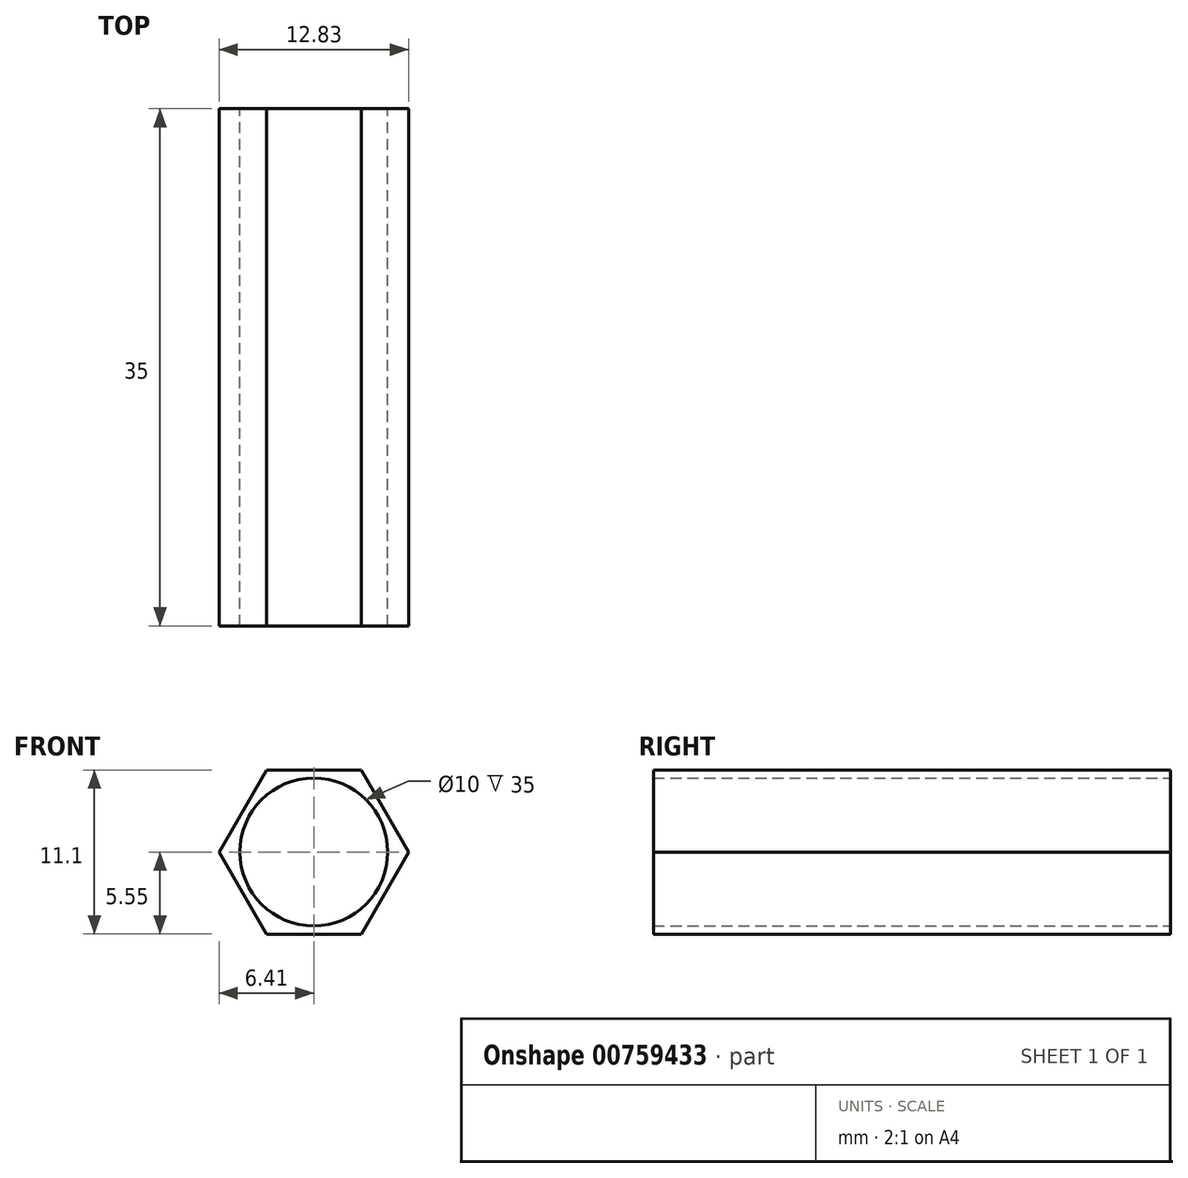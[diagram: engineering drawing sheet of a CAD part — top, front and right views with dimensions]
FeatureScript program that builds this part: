
annotation { "Feature Type Name" : "Feature", "Feature Type Description" : "" }
export const myFeature = defineFeature(function(context is Context, id is Id, definition is map)
    precondition{}
    {
        {
            var Q0;
            Q0=qCreatedBy(makeId("Front.planeOp"),FACE);
            var sketch = newSketch(context, id + "F0", { "sketchPlane" : qUnion([Q0])});
            skCircle(sketch, "E0", {"center": v(0, 0) * mm, "radius": 5 * mm});
            skLineSegment(sketch, "E1", {"start": v(6.42, 0) * mm, "end": v(3.21, -5.56) * mm});
            skLineSegment(sketch, "E2", {"start": v(3.21, -5.56) * mm, "end": v(-3.2, -5.56) * mm});
            skLineSegment(sketch, "E3", {"start": v(-3.2, -5.56) * mm, "end": v(-6.4, 0) * mm});
            skLineSegment(sketch, "E4", {"start": v(-6.4, 0) * mm, "end": v(-3.2, 5.56) * mm});
            skLineSegment(sketch, "E5", {"start": v(-3.2, 5.55) * mm, "end": v(3.21, 5.55) * mm});
            skLineSegment(sketch, "E6", {"start": v(3.21, 5.55) * mm, "end": v(6.42, 0) * mm});
            skSolve(sketch);
        }
        {
            var Q0;
            Q0 = qSketchRegion(id + "F0", true);
            extrude(context, id + "F1", {"entities" : qUnion([Q0]), "endBound" : BoundingType.SYMMETRIC, "depth" : 35 * mm, "offsetDistance" : 25 * mm});
        }
    });
